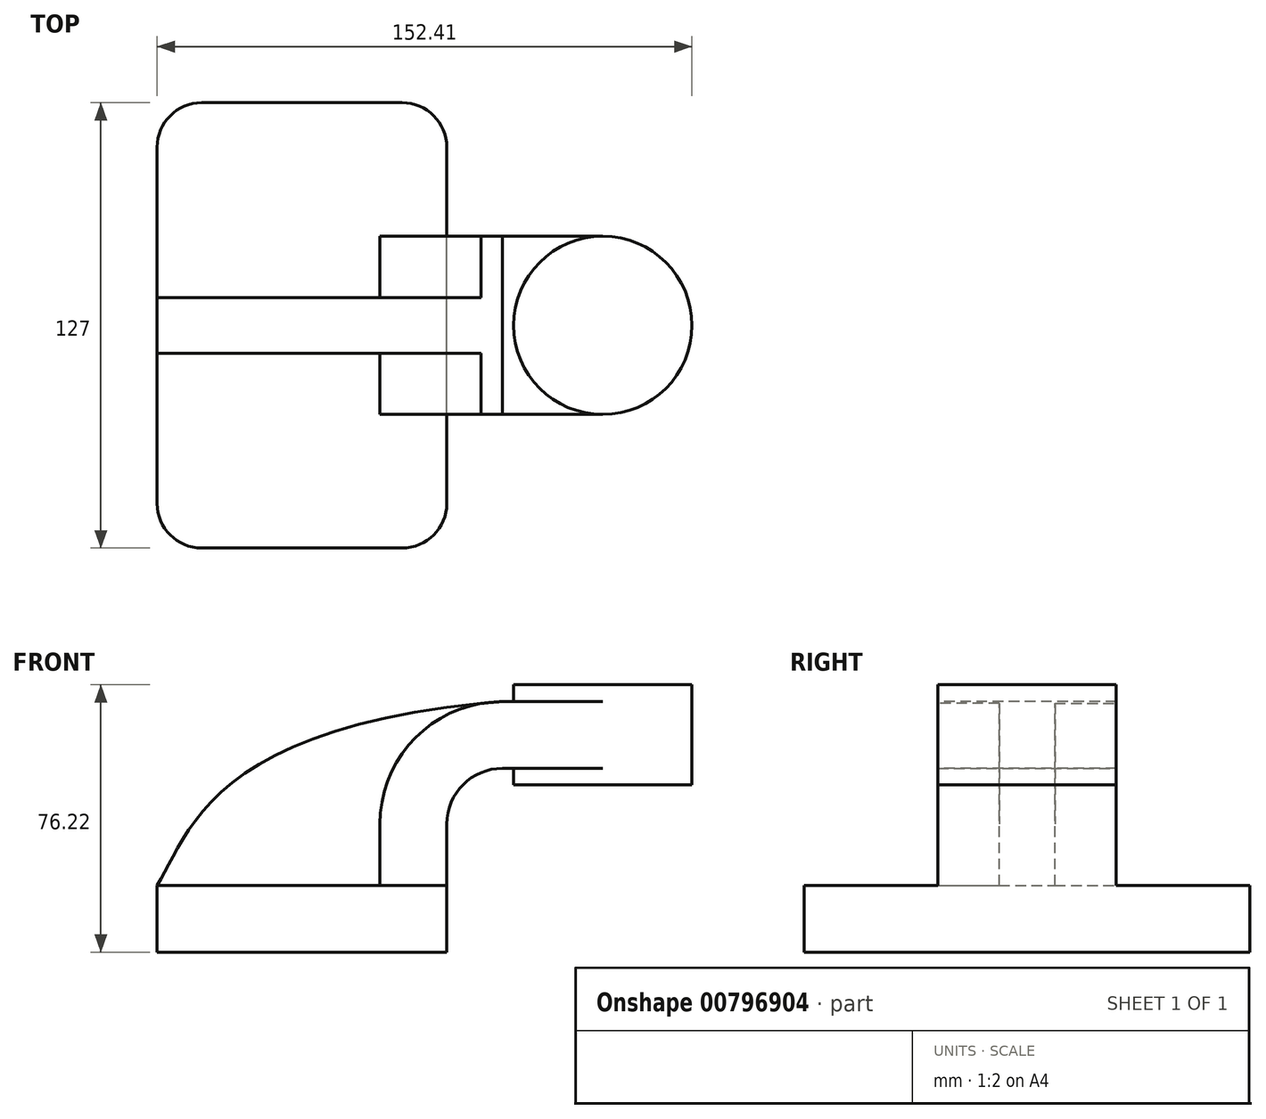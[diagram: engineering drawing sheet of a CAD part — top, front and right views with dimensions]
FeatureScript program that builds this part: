
annotation { "Feature Type Name" : "Feature", "Feature Type Description" : "" }
export const myFeature = defineFeature(function(context is Context, id is Id, definition is map)
    precondition{}
    {
        {
            var Q0;
            Q0=qCreatedBy(makeId("Front.planeOp"),FACE);
            var sketch = newSketch(context, id + "F0", { "sketchPlane" : qUnion([Q0])});
            skLineSegment(sketch, "E0.bottom", {"start": v(-41.28, 9.52) * mm, "end": v(41.27, 9.53) * mm});
            skLineSegment(sketch, "E0.top", {"start": v(-41.28, -9.53) * mm, "end": v(41.28, -9.53) * mm});
            skLineSegment(sketch, "E0.left", {"start": v(-41.28, 9.52) * mm, "end": v(-41.28, -9.53) * mm});
            skLineSegment(sketch, "E0.right", {"start": v(41.27, 9.53) * mm, "end": v(41.28, -9.52) * mm});
            skPoint(sketch, "E0.middle", {"position": v(0, 0) * mm});
            skPoint(sketch, "E1.middle", {"position": v(85.72, 52.4) * mm});
            skLineSegment(sketch, "E2", {"start": v(41.27, 9.53) * mm, "end": v(41.27, 27) * mm});
            skArc(sketch, "E3", {"start": v(41.27, 27) * mm, "mid": v(45.92, 38.23) * mm, "end": v(57.15, 42.88) * mm});
            skLineSegment(sketch, "E4", {"start": v(57.15, 42.88) * mm, "end": v(85.72, 42.88) * mm});
            skLineSegment(sketch, "E5.0", {"start": v(57.15, 61.93) * mm, "end": v(85.72, 61.93) * mm});
            skArc(sketch, "E5.1", {"start": v(22.22, 27) * mm, "mid": v(32.45, 51.7) * mm, "end": v(57.15, 61.93) * mm});
            skLineSegment(sketch, "E5.2", {"start": v(22.22, 9.53) * mm, "end": v(22.22, 27) * mm});
            skFitSpline(sketch, "E6", {"points": [v(-41.28, 9.52) * mm, v(57.15, 61.93) * mm], "startDerivative": vector(25.85, 40.12) * mm, "endDerivative": vector(253.52, 19.97) * mm});
            skLineSegment(sketch, "E7", {"start": v(85.72, 61.93) * mm, "end": v(85.72, 42.88) * mm});
            skPoint(sketch, "E1.right.end.orphan", {"position": v(102.07, 66.88) * mm});
            skPoint(sketch, "E1.bottom.end.orphan", {"position": v(111.12, 38.11) * mm});
            skPoint(sketch, "E8.orphan", {"position": v(69.38, 37.93) * mm});
            skPoint(sketch, "E9.orphan", {"position": v(60.32, 66.69) * mm});
            skLineSegment(sketch, "E10.bottom", {"start": v(111.12, 38.11) * mm, "end": v(60.32, 38.11) * mm});
            skLineSegment(sketch, "E10.top", {"start": v(111.12, 66.69) * mm, "end": v(60.32, 66.69) * mm});
            skLineSegment(sketch, "E10.left", {"start": v(111.12, 38.11) * mm, "end": v(111.12, 66.69) * mm});
            skLineSegment(sketch, "E10.right", {"start": v(60.32, 38.11) * mm, "end": v(60.32, 66.69) * mm});
            skLineSegment(sketch, "E11", {"start": v(85.72, 66.69) * mm, "end": v(85.72, 38.11) * mm});
            skSolve(sketch);
        }
        {
            var Q0;
            Q0=makeQuery(id+"F0.imprint","IMPRINT",FACE,{"disambiguationData":[TD([[makeQuery(id+"F0.imprint","IMPRINT",EDGE,{"derivedFrom":sQuery(id+"F0.wireOp",EDGE,"E0.top")}),1.0]])]});
            extrude(context, id + "F1", {"entities" : qUnion([Q0]), "endBound" : BoundingType.SYMMETRIC, "depth" : 127 * mm, "offsetDistance" : 25.4 * mm});
        }
        {
            var Q0;
            {var subQ1=sQuery(id+"F0.wireOp",EDGE,"E2");Q0=makeQuery(id+"F0.imprint","IMPRINT",FACE,{"disambiguationData":[TD([[makeQuery(id+"F0.imprint","IMPRINT",EDGE,{"derivedFrom":subQ1}),1.0]])]});}
            extrude(context, id + "F2", {"entities" : qUnion([Q0]), "operationType" : NewBodyOperationType.ADD, "endBound" : BoundingType.SYMMETRIC, "depth" : 50.8 * mm, "offsetDistance" : 25.4 * mm});
        }
        {
            var Q0;
            {var subQ5=sQuery(id+"F0.wireOp",EDGE,"E7");Q0=makeQuery(id+"F0.imprint","IMPRINT",FACE,{"disambiguationData":[TD([[makeQuery(id+"F0.imprint","IMPRINT",EDGE,{"derivedFrom":subQ5}),-1.0]])]});}
            extrude(context, id + "F3", {"entities" : qUnion([Q0]), "operationType" : NewBodyOperationType.ADD, "endBound" : BoundingType.SYMMETRIC, "depth" : 50.8 * mm, "offsetDistance" : 25.4 * mm});
        }
        {
            var Q0;
            {var subQ3=sQuery(id+"F0.wireOp",EDGE,"E5.2");Q0=makeQuery(id+"F0.imprint","IMPRINT",FACE,{"disambiguationData":[TD([[makeQuery(id+"F0.imprint","IMPRINT",EDGE,{"derivedFrom":subQ3}),1.0]])]});}
            extrude(context, id + "F4", {"entities" : qUnion([Q0]), "operationType" : NewBodyOperationType.ADD, "endBound" : BoundingType.SYMMETRIC, "depth" : 15.88 * mm, "offsetDistance" : 25.4 * mm});
        }
        {
            var Q0;
            {var subQ0=sQuery(id+"F0.wireOp",EDGE,"E11");var subQ1=sQuery(id+"F0.wireOp",EDGE,"E4");var subQ2=makeQuery(id+"F0.imprint","INTERSECT",VERTEX,{"derivedFrom":[subQ1,subQ0]});Q0=makeQuery(id+"F0.imprint","IMPRINT",FACE,{"disambiguationData":[TD([[makeQuery(id+"F0.imprint","IMPRINT",EDGE,{"disambiguationData":[TD([[subQ2,1.0]])],"derivedFrom":subQ1}),1.0]])]});}
            extrude(context, id + "F5", {"entities" : qUnion([Q0]), "operationType" : NewBodyOperationType.ADD, "endBound" : BoundingType.SYMMETRIC, "depth" : 50.8 * mm, "offsetDistance" : 25.4 * mm});
        }
        {
            var Q0;
            {var subQ4=sQuery(id+"F0.wireOp",EDGE,"E10.left");Q0=makeQuery(id+"F0.imprint","IMPRINT",FACE,{"disambiguationData":[TD([[makeQuery(id+"F0.imprint","IMPRINT",EDGE,{"derivedFrom":subQ4}),1.0]])]});}
            var Q1;
            Q1=sQuery(id+"F0.wireOp",EDGE,"E11");
            revolve(context, id + "F6", {"operationType" : NewBodyOperationType.ADD, "surfaceOperationType" : NewSurfaceOperationType.NEW, "entities" : qUnion([Q0]), "axis" : qUnion([Q1]), "revolveType" : RevolveType.FULL});
        }
        {
            var Q0;
            Q0=makeQuery(id+"F1.opExtrude","CAP_EDGE",EDGE,{"disambiguationData":[OSD([sQuery(id+"F0.wireOp",EDGE,"E0.left")])],"isStart":false});
            var Q1;
            Q1=makeQuery(id+"F1.opExtrude","CAP_EDGE",EDGE,{"disambiguationData":[OSD([sQuery(id+"F0.wireOp",EDGE,"E0.right")])],"isStart":false});
            var Q2;
            Q2=makeQuery(id+"F1.opExtrude","CAP_EDGE",EDGE,{"disambiguationData":[OSD([sQuery(id+"F0.wireOp",EDGE,"E0.right")])],"isStart":true});
            var Q3;
            Q3=makeQuery(id+"F1.opExtrude","CAP_EDGE",EDGE,{"disambiguationData":[OSD([sQuery(id+"F0.wireOp",EDGE,"E0.left")])],"isStart":true});
            fillet(context, id + "F7", {"entities" : qUnion([Q0, Q1, Q2, Q3]), "radius" : 12.7 * mm, "tangentPropagation" : true, "allowEdgeOverflow" : false});
        }
    });
